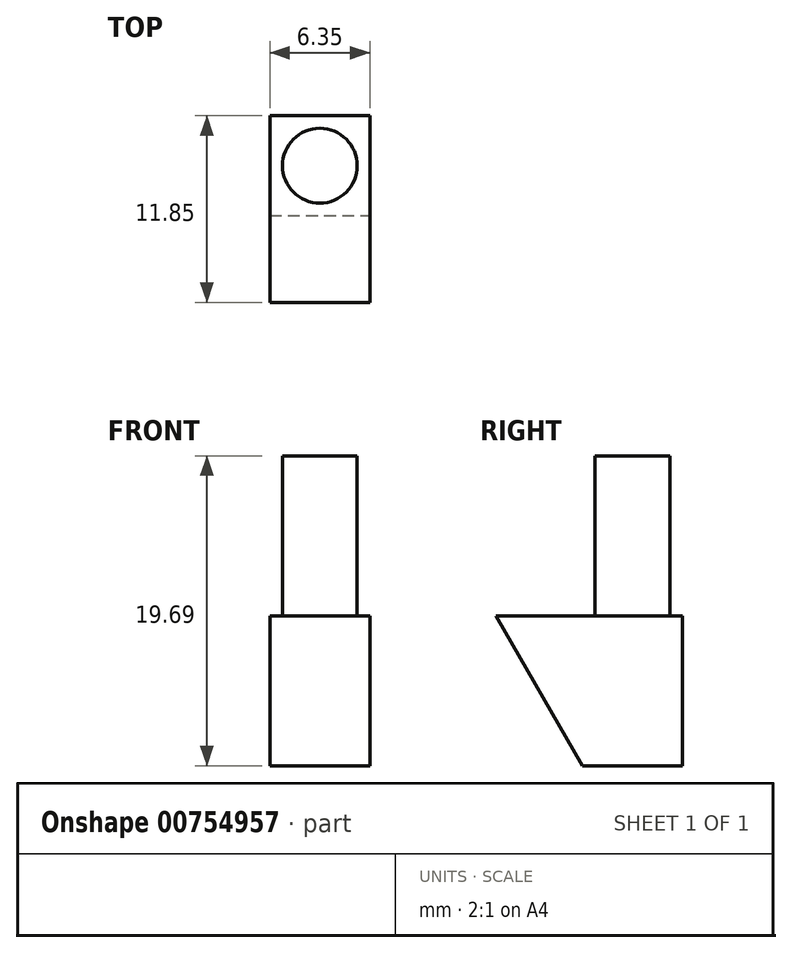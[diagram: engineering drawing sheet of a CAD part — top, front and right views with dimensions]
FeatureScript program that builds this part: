
annotation { "Feature Type Name" : "Feature", "Feature Type Description" : "" }
export const myFeature = defineFeature(function(context is Context, id is Id, definition is map)
    precondition{}
    {
        {
            var Q0;
            Q0=qCreatedBy(makeId("Top.planeOp"),FACE);
            var sketch = newSketch(context, id + "F0", { "sketchPlane" : qUnion([Q0])});
            skLineSegment(sketch, "E0.bottom", {"start": v(0, 0) * mm, "end": v(6.35, 0) * mm});
            skLineSegment(sketch, "E0.top", {"start": v(0, 6.35) * mm, "end": v(6.35, 6.35) * mm});
            skLineSegment(sketch, "E0.left", {"start": v(0, 0) * mm, "end": v(0, 6.35) * mm});
            skLineSegment(sketch, "E0.right", {"start": v(6.35, 0) * mm, "end": v(6.35, 6.35) * mm});
            skSolve(sketch);
        }
        {
            var Q0;
            Q0=makeQuery(id+"F0.imprint","IMPRINT",FACE,{"disambiguationData":[TD([[makeQuery(id+"F0.imprint","IMPRINT",EDGE,{"derivedFrom":sQuery(id+"F0.wireOp",EDGE,"E0.bottom")}),1.0]])]});
            extrude(context, id + "F1", {"entities" : qUnion([Q0]), "depth" : 9.52 * mm, "offsetDistance" : 25.4 * mm});
        }
        {
            var Q0;
            Q0=makeQuery(id+"F1.opExtrude","CAP_FACE",FACE,{"disambiguationData":[OSD([sQuery(id+"F0.wireOp",EDGE,"E0.bottom"),sQuery(id+"F0.wireOp",EDGE,"E0.top"),sQuery(id+"F0.wireOp",EDGE,"E0.left"),sQuery(id+"F0.wireOp",EDGE,"E0.right")])],"isStart":false});
            var sketch = newSketch(context, id + "F2", { "sketchPlane" : qUnion([Q0])});
            skLineSegment(sketch, "E1", {"start": v(0, 3.17) * mm, "end": v(6.35, 3.17) * mm, "construction": true});
            skCircle(sketch, "E2", {"center": v(3.18, 3.17) * mm, "radius": 2.37 * mm});
            skSolve(sketch);
        }
        {
            var Q0;
            Q0=makeQuery(id+"F2.imprint","IMPRINT",FACE,{"disambiguationData":[TD([[makeQuery(id+"F2.imprint","IMPRINT",EDGE,{"derivedFrom":sQuery(id+"F2.wireOp",EDGE,"E2")}),1.0]])]});
            extrude(context, id + "F3", {"entities" : qUnion([Q0]), "operationType" : NewBodyOperationType.ADD, "depth" : 10.16 * mm, "offsetDistance" : 25.4 * mm});
        }
        {
            var Q0;
            Q0=makeQuery(id+"F1.opExtrude","SWEPT_FACE",FACE,{"disambiguationData":[OSD([sQuery(id+"F0.wireOp",EDGE,"E0.left")])]});
            var sketch = newSketch(context, id + "F4", { "sketchPlane" : qUnion([Q0])});
            skLineSegment(sketch, "E3.0", {"start": v(0, 9.53) * mm, "end": v(0, 0) * mm});
            skLineSegment(sketch, "E4", {"start": v(0, 9.53) * mm, "end": v(5.5, 9.53) * mm});
            skLineSegment(sketch, "E5", {"start": v(5.5, 9.53) * mm, "end": v(0, 0) * mm});
            skSolve(sketch);
        }
        {
            var Q0;
            Q0=makeQuery(id+"F4.imprint","IMPRINT",FACE,{"disambiguationData":[TD([[makeQuery(id+"F4.imprint","IMPRINT",EDGE,{"derivedFrom":sQuery(id+"F4.wireOp",EDGE,"E3.0")}),1.0]])]});
            var Q1;
            Q1=makeQuery(id+"F1.opExtrude","SWEPT_FACE",FACE,{"disambiguationData":[OSD([sQuery(id+"F0.wireOp",EDGE,"E0.right")])]});
            extrude(context, id + "F5", {"entities" : qUnion([Q0]), "operationType" : NewBodyOperationType.ADD, "endBound" : BoundingType.UP_TO_SURFACE, "oppositeDirection" : true, "depth" : 25.4 * mm, "endBoundEntityFace" : qUnion([Q1]), "offsetDistance" : 25.4 * mm});
        }
    });
